# Revit family: ASH_ArmitageShanks_CounterTopWashBasins_Profile21-50cm
name_source: partatom
category: Plumbing Fixtures
revit_build: Autodesk Revit MEP 2012 (Build: 20110309_2315(x64)
units: mm (PartAtom-declared; Revit-internal decimal feet)

## types (4) — shared parameters
Accessories = www.idealspec.co.uk
AreaUnits = millimeters
Assembly Code = C1030200
AssetType = Fixed
BasinMaterial = ASH_ArmitageShanks _Sanitaryware_White4_Render
Brand = Armitage Shanks
Category = SanitaryTerminal_WASHHANDBASIN_UK
Color = White
ConnectionType = Plumbing
Default Elevation = 1219 mm
DrainSize = 32 mm  [stored 0.104987 ft]
DurationUnit = year
ECA = Yes
ExpectedLife = 30
Finish = White
IfcExportAs = IfcSanitaryTerminalType
IfcExportType = WASHHANDBASIN
InstallationInstructions = www.idealspec.co.uk/resources.html
LinearUnits = millimeters
ManufacturerURL = www.idealspec.co.uk
Material = Vitreous china
NBSDescription = Counter top wash basins
NBSReference = 35-70-70/360
NettWeight = 12 Kg
NominalDepth = 412 mm
NominalHeight = 200 mm
NominalLength = 412 mm
NominalWidth = 500 mm
Shape = Sculptured
Size = 500 x 412 x 200 mm
Space = Internal
SpareParts = www.fastpart-spares.co.uk
URL = www.idealspec.co.uk
Uniclass2 = Pr_40_20_96_18
Version = 1
VolumeUnits = Litres
WRAS = Yes
WarrantyDescription = Manufacturers warranty
WarrantyDurationParts = 99
WarrantyDurationUnit = year
WashHandBasinMounting = CounterTop
WashHandBasinType = HANDRINSE
WaterEfficientProduct = Yes
zero-valued in all types: CWFU, HWFU, WFU

## per-type parameters (varying)
| type | 1TH | 2TH | BIMObjectName | Description | Features | Model | ModelNumber | ModelReference | Name | ProductInformation |
| S249201 - Profile 21 50cm Semi-Countertop Washbasin 1 Taphole With Overflow | Yes | No | ASH_ArmitageShanks_CounterTopWashBasins_Profile21_S2492 | Profile 21 50 cm semi-countertop washbasin 1 taphole with overflow | 50 cm semi-countertop washbasin 1 taphole with overflow | S249201 | S249201 | Profile 21 50 cm semi-countertop washbasin 1 taphole with overflow | CounterTopWashBasins_Profile21_S2492_ArmitageShanks | www.idealspec.co.uk/assets/datasheet/S249201 |
| S249301 - Profile 21 50cm Semi-Countertop Washbasin 1 Taphole No Overflow | Yes | No | ASH_ArmitageShanks_CounterTopWashBasins_Profile21_S2493 | Profile 21 50 cm semi-countertop washbasin 1 taphole no overflow | 50 cm semi-countertop washbasin 1 taphole no overflow | S249301 | S249301 | Profile 21 50 cm semi-countertop washbasin 1 taphole no overflow | CounterTopWashBasins_Profile21_S2493_ArmitageShanks | www.idealspec.co.uk/assets/datasheet/S249301 |
| S249401 - Profile 21 50cm Semi-Countertop Washbasin 2 Tapholes Overflow and Chainstay hole | No | Yes | ASH_ArmitageShanks_CounterTopWashBasins_Profile21_S2494 | Profile 21 50 cm semi-countertop washbasin 2 tapholes overflow and chainstay hole | 50 cm semi-countertop washbasin 2 tapholes overflow and chainstay hole | S249401 | S249401 | Profile 21 50 cm semi-countertop washbasin 2 tapholes overflow and chainstay hole | CounterTopWashBasins_Profile21_S2494_ArmitageShanks | www.idealspec.co.uk/assets/datasheet/S249401 |
| S249501 - Profile 21 50cm Semi-Countertop Washbasin 2 Taphole No Overflow With Chainstay Hole | No | Yes | ASH_ArmitageShanks_CounterTopWashBasins_Profile21_S2495 | Profile 21 50 cm semi-countertop washbasin 2 taphole no overflow with chainstay hole | 50 cm semi-countertop washbasin 2 taphole no overflow with chainstay hole | S249501 | S249501 | Profile 21 50 cm semi-countertop washbasin 2 taphole no overflow with chainstay hole | CounterTopWashBasins_Profile21_S2495_ArmitageShanks | www.idealspec.co.uk/assets/datasheet/S249501 |

note: [stored X ft] marks values corroborated as IEEE doubles in the binary element streams (Revit-internal decimal feet)

## geometry (parser evidence)
native form markers: Blend x2, Sweep x3
no freeform markers — native parametric forms only
